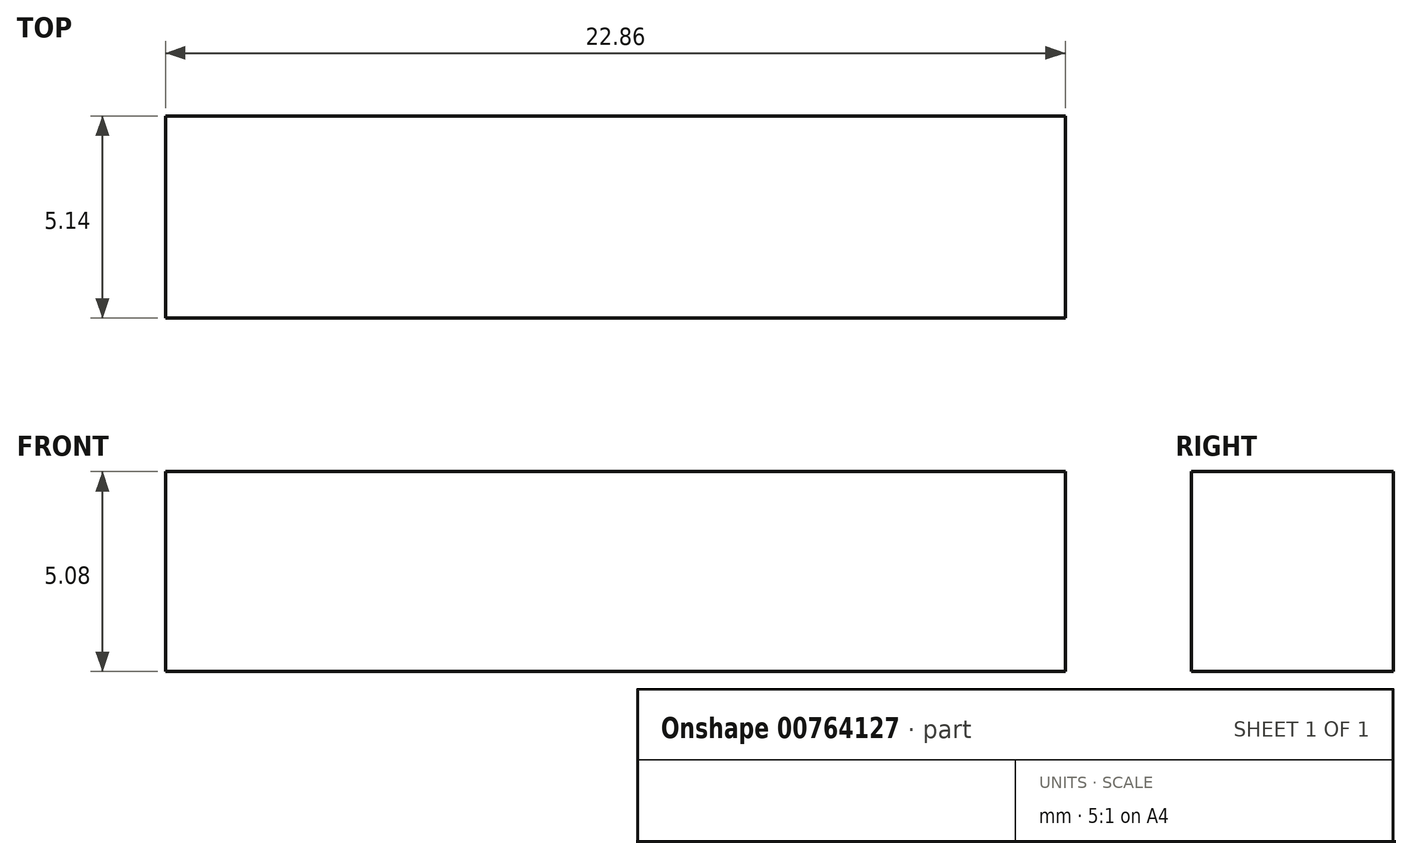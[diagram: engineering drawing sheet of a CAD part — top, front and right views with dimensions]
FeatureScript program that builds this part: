
annotation { "Feature Type Name" : "Feature", "Feature Type Description" : "" }
export const myFeature = defineFeature(function(context is Context, id is Id, definition is map)
    precondition{}
    {
        {
            var Q0;
            Q0=qCreatedBy(makeId("Top.planeOp"),FACE);
            var sketch = newSketch(context, id + "F0", { "sketchPlane" : qUnion([Q0])});
            skLineSegment(sketch, "E0.bottom", {"start": v(33.78, -17.68) * mm, "end": v(-33.78, -17.68) * mm});
            skLineSegment(sketch, "E0.top", {"start": v(33.78, 17.68) * mm, "end": v(-33.78, 17.68) * mm});
            skLineSegment(sketch, "E0.left", {"start": v(33.78, -17.68) * mm, "end": v(33.78, 17.68) * mm});
            skLineSegment(sketch, "E0.right", {"start": v(-33.78, -17.68) * mm, "end": v(-33.78, 17.68) * mm});
            skPoint(sketch, "E0.middle", {"position": v(0, 0) * mm});
            skLineSegment(sketch, "E1", {"start": v(-28.04, 12.6) * mm, "end": v(-28.04, -17.68) * mm});
            skLineSegment(sketch, "E2", {"start": v(-28.04, -17.68) * mm, "end": v(-28.04, 12.6) * mm});
            skLineSegment(sketch, "E3", {"start": v(-33.78, 12.6) * mm, "end": v(10.66, 12.6) * mm});
            skLineSegment(sketch, "E4", {"start": v(-5.18, 12.6) * mm, "end": v(-5.18, -12.35) * mm});
            skLineSegment(sketch, "E5", {"start": v(30.73, 17.68) * mm, "end": v(30.73, -17.68) * mm});
            skLineSegment(sketch, "E6", {"start": v(-28.04, -12.35) * mm, "end": v(33.78, -12.35) * mm});
            skLineSegment(sketch, "E7", {"start": v(-28.04, 12.6) * mm, "end": v(-5.18, -12.35) * mm});
            skLineSegment(sketch, "E8", {"start": v(10.66, 17.68) * mm, "end": v(10.66, -12.35) * mm});
            skLineSegment(sketch, "E9", {"start": v(10.66, -12.35) * mm, "end": v(10.66, 12.6) * mm});
            skLineSegment(sketch, "E10", {"start": v(10.66, 12.6) * mm, "end": v(-33.78, 12.6) * mm});
            skLineSegment(sketch, "E11", {"start": v(3.16, 12.6) * mm, "end": v(3.16, -12.35) * mm});
            skLineSegment(sketch, "E12.trimOffspring", {"start": v(30.73, 12.6) * mm, "end": v(33.78, 12.6) * mm});
            skLineSegment(sketch, "E13", {"start": v(-5.18, -17.68) * mm, "end": v(-5.18, -22.82) * mm});
            skLineSegment(sketch, "E14", {"start": v(-28.04, -17.68) * mm, "end": v(-28.04, -22.82) * mm});
            skLineSegment(sketch, "E15", {"start": v(-33.78, -17.68) * mm, "end": v(-33.78, -22.82) * mm});
            skLineSegment(sketch, "E16", {"start": v(30.73, -17.68) * mm, "end": v(30.73, -22.82) * mm});
            skLineSegment(sketch, "E17", {"start": v(33.78, -17.68) * mm, "end": v(33.78, -22.82) * mm});
            skLineSegment(sketch, "E18", {"start": v(30.73, -22.82) * mm, "end": v(33.78, -22.82) * mm});
            skPoint(sketch, "E19.orphan", {"position": v(-33.78, -24.24) * mm});
            skPoint(sketch, "E20.orphan", {"position": v(-5.18, -24.24) * mm});
            skLineSegment(sketch, "E21", {"start": v(-33.78, -22.82) * mm, "end": v(-5.18, -22.82) * mm});
            skSolve(sketch);
        }
        {
            var Q0;
            {var subQ2=sQuery(id+"F0.wireOp",EDGE,"E13");Q0=makeQuery(id+"F0.imprint","IMPRINT",FACE,{"disambiguationData":[TD([[makeQuery(id+"F0.imprint","IMPRINT",EDGE,{"derivedFrom":subQ2}),-1.0]])]});}
            extrude(context, id + "F1", {"entities" : qUnion([Q0]), "depth" : 5.08 * mm, "offsetDistance" : 25.4 * mm});
        }
    });
